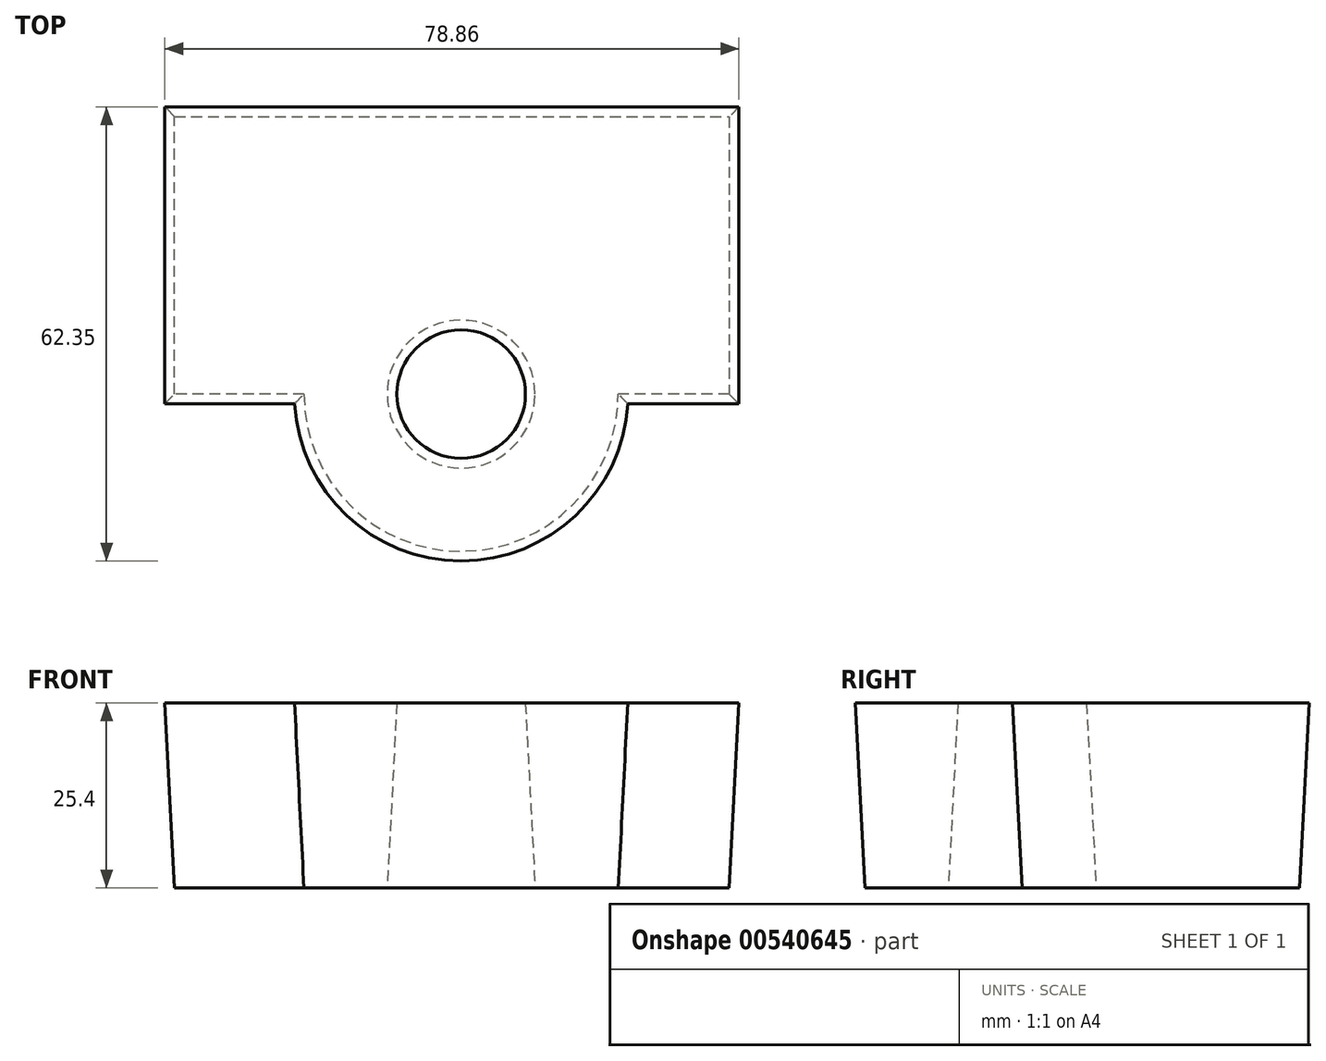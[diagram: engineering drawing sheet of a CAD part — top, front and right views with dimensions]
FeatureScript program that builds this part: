
annotation { "Feature Type Name" : "Feature", "Feature Type Description" : "" }
export const myFeature = defineFeature(function(context is Context, id is Id, definition is map)
    precondition{}
    {
        {
            var Q0;
            Q0=qCreatedBy(makeId("Top.planeOp"),FACE);
            var sketch = newSketch(context, id + "F0", { "sketchPlane" : qUnion([Q0])});
            skLineSegment(sketch, "E0.bottom", {"start": v(-35.65, 18.35) * mm, "end": v(40.55, 18.35) * mm});
            skLineSegment(sketch, "E0.top", {"start": v(-35.65, -19.75) * mm, "end": v(-17.87, -19.75) * mm});
            skLineSegment(sketch, "E0.left", {"start": v(-35.65, 18.35) * mm, "end": v(-35.65, -19.75) * mm});
            skLineSegment(sketch, "E0.right", {"start": v(40.55, 18.35) * mm, "end": v(40.55, -19.75) * mm});
            skArc(sketch, "E1", {"start": v(-17.87, -19.75) * mm, "mid": v(3.72, -41.34) * mm, "end": v(25.3, -19.75) * mm});
            skCircle(sketch, "E2", {"center": v(3.72, -19.75) * mm, "radius": 10.16 * mm});
            skLineSegment(sketch, "E3.trimOffspring", {"start": v(25.3, -19.75) * mm, "end": v(40.55, -19.75) * mm});
            skSolve(sketch);
        }
        {
            var Q0;
            Q0=makeQuery(id+"F0.imprint","IMPRINT",FACE,{"disambiguationData":[TD([[makeQuery(id+"F0.imprint","IMPRINT",EDGE,{"derivedFrom":sQuery(id+"F0.wireOp",EDGE,"E0.bottom")}),-1.0]])]});
            extrude(context, id + "F1", {"entities" : qUnion([Q0]), "depth" : 25.4 * mm, "offsetDistance" : 25.4 * mm, "hasDraft" : true, "draftAngle" : 3 * degree});
        }
    });
